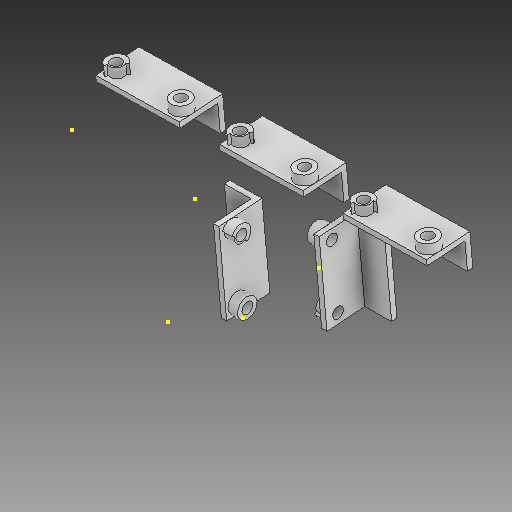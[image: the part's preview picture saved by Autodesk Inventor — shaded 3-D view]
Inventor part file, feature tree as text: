
AUTODESK INVENTOR PART (.ipt)
format: ipt  version: 2020 (Build 240168000, 168)  size: 226,304 bytes
history: native  units: mm
features: sketch x5, other x3
ambient origin geometry x8: Origin, YZ Plane, XZ Plane, XY Plane, X Axis, Y Axis, Z Axis, Center Point
bodies: Solid1 (feature_tree)
feature tree (8):
  other  "5DržačaLidara.ipt"
  other  "Solid1::5DržačaLidara.ipt"
  other  "TaggingFeature1"
  sketch  "Sketch8"
  sketch  "Sketch8_1"  dims[d0=10.0mm]
  sketch  "Sketch8_2"
  sketch  "Sketch8_3"
  sketch  "Sketch8_4"
